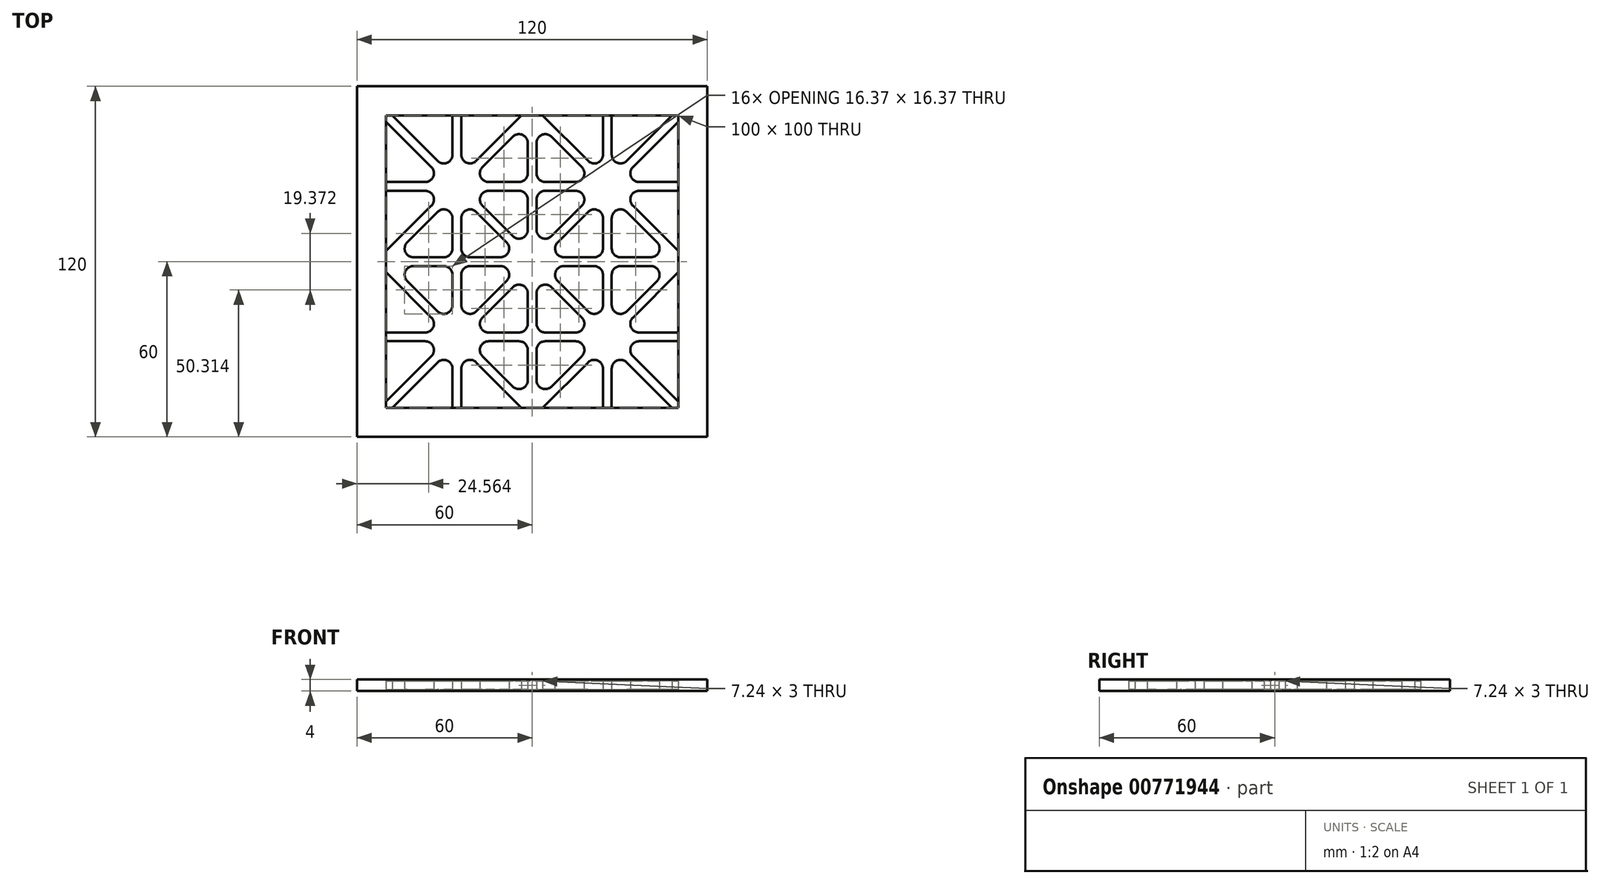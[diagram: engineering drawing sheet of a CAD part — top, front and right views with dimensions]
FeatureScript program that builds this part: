
annotation { "Feature Type Name" : "Feature", "Feature Type Description" : "" }
export const myFeature = defineFeature(function(context is Context, id is Id, definition is map)
    precondition{}
    {
        {
            var Q0;
            Q0=qCreatedBy(makeId("Top.planeOp"),FACE);
            var sketch = newSketch(context, id + "F0", { "sketchPlane" : qUnion([Q0])});
            skLineSegment(sketch, "E0.bottom", {"start": v(0, 0) * mm, "end": v(120, 0) * mm});
            skLineSegment(sketch, "E0.top", {"start": v(0, 120) * mm, "end": v(120, 120) * mm});
            skLineSegment(sketch, "E0.left", {"start": v(0, 0) * mm, "end": v(0, 120) * mm});
            skLineSegment(sketch, "E0.right", {"start": v(120, 0) * mm, "end": v(120, 120) * mm});
            skLineSegment(sketch, "E1.0", {"start": v(10, 10) * mm, "end": v(10, 110) * mm});
            skLineSegment(sketch, "E1.1", {"start": v(10, 10) * mm, "end": v(110, 10) * mm});
            skLineSegment(sketch, "E1.2", {"start": v(110, 10) * mm, "end": v(110, 110) * mm});
            skLineSegment(sketch, "E1.3", {"start": v(10, 110) * mm, "end": v(110, 110) * mm});
            skSolve(sketch);
        }
        {
            var Q0;
            Q0 = qSketchRegion(id + "F0", true);
            extrude(context, id + "F1", {"entities" : qUnion([Q0]), "depth" : 2 * mm, "offsetDistance" : 25 * mm, "hasSecondDirection" : true, "secondDirectionOppositeDirection" : true, "secondDirectionDepth" : 2 * mm});
        }
        {
            var Q0;
            Q0=qCreatedBy(makeId("Top.planeOp"),FACE);
            var sketch = newSketch(context, id + "F2", { "sketchPlane" : qUnion([Q0])});
            skLineSegment(sketch, "E2.0", {"start": v(10, 10) * mm, "end": v(10, 110) * mm, "construction": true});
            skLineSegment(sketch, "E2.1", {"start": v(10, 110) * mm, "end": v(110, 110) * mm, "construction": true});
            skLineSegment(sketch, "E2.2", {"start": v(110, 10) * mm, "end": v(110, 110) * mm, "construction": true});
            skLineSegment(sketch, "E2.3", {"start": v(10, 10) * mm, "end": v(110, 10) * mm, "construction": true});
            skLineSegment(sketch, "E3", {"start": v(10, 60) * mm, "end": v(110, 60) * mm, "construction": true});
            skLineSegment(sketch, "E4", {"start": v(60, 10) * mm, "end": v(60, 110) * mm, "construction": true});
            skLineSegment(sketch, "E5.0", {"start": v(12.12, 58.5) * mm, "end": v(32.75, 58.5) * mm});
            skLineSegment(sketch, "E6.MirrorCS", {"start": v(12.12, 61.5) * mm, "end": v(32.75, 61.5) * mm});
            skLineSegment(sketch, "E7.0", {"start": v(61.5, 10) * mm, "end": v(61.5, 32.75) * mm});
            skLineSegment(sketch, "E8.MirrorCS", {"start": v(58.5, 12.12) * mm, "end": v(58.5, 32.75) * mm});
            skLineSegment(sketch, "E9", {"start": v(10, 10) * mm, "end": v(58.5, 58.5) * mm, "construction": true});
            skLineSegment(sketch, "E10.trimOffspring", {"start": v(58.5, 63.62) * mm, "end": v(58.5, 84.25) * mm});
            skLineSegment(sketch, "E11.trimOffspring", {"start": v(63.62, 58.5) * mm, "end": v(84.25, 58.5) * mm});
            skLineSegment(sketch, "E12.trimOffspring", {"start": v(61.5, 63.62) * mm, "end": v(61.5, 84.25) * mm});
            skLineSegment(sketch, "E13.trimOffspring", {"start": v(63.62, 61.5) * mm, "end": v(84.25, 61.5) * mm});
            skLineSegment(sketch, "E14.0", {"start": v(12.12, 10) * mm, "end": v(32.75, 30.63) * mm});
            skLineSegment(sketch, "E15.MirrorCS", {"start": v(10, 12.12) * mm, "end": v(30.63, 32.75) * mm});
            skLineSegment(sketch, "E16", {"start": v(58.5, 10) * mm, "end": v(35.31, 33.19) * mm, "construction": true});
            skLineSegment(sketch, "E17.0", {"start": v(58.5, 12.12) * mm, "end": v(37.87, 32.75) * mm});
            skLineSegment(sketch, "E18.MirrorCS", {"start": v(56.38, 10) * mm, "end": v(35.75, 30.63) * mm});
            skLineSegment(sketch, "E19.trimOffspring", {"start": v(37.87, 35.75) * mm, "end": v(58.5, 56.38) * mm});
            skLineSegment(sketch, "E20.MirrorCS", {"start": v(12.12, 58.5) * mm, "end": v(32.75, 37.87) * mm});
            skLineSegment(sketch, "E21.MirrorCS", {"start": v(10, 56.38) * mm, "end": v(30.63, 35.75) * mm});
            skLineSegment(sketch, "E22.trimOffspring", {"start": v(35.75, 37.87) * mm, "end": v(56.38, 58.5) * mm});
            skPoint(sketch, "E23.orphan", {"position": v(10, 58.5) * mm});
            skLineSegment(sketch, "E24.1.0", {"start": v(32.75, 58.5) * mm, "end": v(32.75, 37.87) * mm});
            skLineSegment(sketch, "E24.1.2", {"start": v(37.87, 35.75) * mm, "end": v(58.5, 35.75) * mm});
            skLineSegment(sketch, "E24.1.3", {"start": v(37.87, 32.75) * mm, "end": v(58.5, 32.75) * mm});
            skLineSegment(sketch, "E24.1.4", {"start": v(35.75, 10) * mm, "end": v(35.75, 30.63) * mm});
            skLineSegment(sketch, "E24.1.5", {"start": v(32.75, 10) * mm, "end": v(32.75, 30.63) * mm});
            skLineSegment(sketch, "E24.1.6", {"start": v(10, 32.75) * mm, "end": v(30.63, 32.75) * mm});
            skLineSegment(sketch, "E24.1.7", {"start": v(10, 35.75) * mm, "end": v(30.63, 35.75) * mm});
            skPoint(sketch, "E24.center", {"position": v(34.25, 34.25) * mm});
            skLineSegment(sketch, "E24.anchor1", {"start": v(34.25, 34.25) * mm, "end": v(12.12, 10) * mm, "construction": true});
            skLineSegment(sketch, "E24.anchor2", {"start": v(34.25, 34.25) * mm, "end": v(1.46, 32.75) * mm, "construction": true});
            skPoint(sketch, "E25.orphan", {"position": v(32.75, 67.04) * mm});
            skPoint(sketch, "E26.orphan", {"position": v(35.75, 67.04) * mm});
            skLineSegment(sketch, "E27.trimOffspring", {"start": v(35.75, 58.5) * mm, "end": v(56.38, 58.5) * mm});
            skLineSegment(sketch, "E28.trimOffspring", {"start": v(35.75, 58.5) * mm, "end": v(35.75, 37.87) * mm});
            skPoint(sketch, "E29.orphan", {"position": v(67.04, 35.75) * mm});
            skLineSegment(sketch, "E30.trimOffspring", {"start": v(58.5, 35.75) * mm, "end": v(58.5, 56.38) * mm});
            skPoint(sketch, "E31.orphan", {"position": v(32.75, 35.75) * mm});
            skPoint(sketch, "E32.orphan", {"position": v(34.25, 36.37) * mm});
            skPoint(sketch, "E33.orphan", {"position": v(35.75, 35.75) * mm});
            skPoint(sketch, "E34.orphan", {"position": v(36.37, 34.25) * mm});
            skPoint(sketch, "E35.orphan", {"position": v(35.75, 32.75) * mm});
            skPoint(sketch, "E36.orphan", {"position": v(34.25, 32.13) * mm});
            skLineSegment(sketch, "E37.trimOffspring", {"start": v(32.75, 32.6) * mm, "end": v(32.75, 32.75) * mm});
            skLineSegment(sketch, "E38.trimOffspring", {"start": v(32.03, 34.15) * mm, "end": v(32.13, 34.25) * mm});
            skLineSegment(sketch, "E39", {"start": v(10, 35.75) * mm, "end": v(10, 32.75) * mm});
            skPoint(sketch, "E40.orphan", {"position": v(1.46, 35.75) * mm});
            skPoint(sketch, "E41.orphan", {"position": v(35.75, 1.46) * mm});
            skPoint(sketch, "E42.orphan", {"position": v(32.75, 1.46) * mm});
            skLineSegment(sketch, "E43.1.0", {"start": v(107.88, 58.5) * mm, "end": v(87.25, 37.87) * mm});
            skLineSegment(sketch, "E43.1.1", {"start": v(110, 56.38) * mm, "end": v(89.37, 35.75) * mm});
            skLineSegment(sketch, "E43.1.2", {"start": v(110, 35.75) * mm, "end": v(89.37, 35.75) * mm});
            skLineSegment(sketch, "E43.1.3", {"start": v(110, 32.75) * mm, "end": v(89.37, 32.75) * mm});
            skLineSegment(sketch, "E43.1.4", {"start": v(110, 12.12) * mm, "end": v(89.37, 32.75) * mm});
            skLineSegment(sketch, "E43.1.5", {"start": v(107.88, 10) * mm, "end": v(87.25, 30.63) * mm});
            skLineSegment(sketch, "E43.1.6", {"start": v(87.25, 10) * mm, "end": v(87.25, 30.63) * mm});
            skLineSegment(sketch, "E43.1.7", {"start": v(84.25, 10) * mm, "end": v(84.25, 30.63) * mm});
            skLineSegment(sketch, "E43.1.8", {"start": v(63.62, 10) * mm, "end": v(84.25, 30.63) * mm});
            skLineSegment(sketch, "E43.1.9", {"start": v(61.5, 12.12) * mm, "end": v(82.13, 32.75) * mm});
            skLineSegment(sketch, "E43.1.10", {"start": v(61.5, 32.75) * mm, "end": v(82.13, 32.75) * mm});
            skLineSegment(sketch, "E43.1.11", {"start": v(61.5, 35.75) * mm, "end": v(82.13, 35.75) * mm});
            skLineSegment(sketch, "E43.1.12", {"start": v(82.13, 35.75) * mm, "end": v(61.5, 56.38) * mm});
            skLineSegment(sketch, "E43.1.13", {"start": v(84.25, 37.87) * mm, "end": v(63.62, 58.5) * mm});
            skLineSegment(sketch, "E43.1.14", {"start": v(84.25, 37.87) * mm, "end": v(84.25, 58.5) * mm});
            skLineSegment(sketch, "E43.1.15", {"start": v(87.25, 37.87) * mm, "end": v(87.25, 58.5) * mm});
            skLineSegment(sketch, "E43.2.0", {"start": v(61.5, 107.88) * mm, "end": v(82.13, 87.25) * mm});
            skLineSegment(sketch, "E43.2.1", {"start": v(63.62, 110) * mm, "end": v(84.25, 89.37) * mm});
            skLineSegment(sketch, "E43.2.2", {"start": v(84.25, 110) * mm, "end": v(84.25, 89.37) * mm});
            skLineSegment(sketch, "E43.2.3", {"start": v(87.25, 110) * mm, "end": v(87.25, 89.37) * mm});
            skLineSegment(sketch, "E43.2.4", {"start": v(107.88, 110) * mm, "end": v(87.25, 89.37) * mm});
            skLineSegment(sketch, "E43.2.5", {"start": v(110, 107.88) * mm, "end": v(89.37, 87.25) * mm});
            skLineSegment(sketch, "E43.2.6", {"start": v(110, 87.25) * mm, "end": v(89.37, 87.25) * mm});
            skLineSegment(sketch, "E43.2.7", {"start": v(110, 84.25) * mm, "end": v(89.37, 84.25) * mm});
            skLineSegment(sketch, "E43.2.8", {"start": v(110, 63.62) * mm, "end": v(89.37, 84.25) * mm});
            skLineSegment(sketch, "E43.2.9", {"start": v(107.88, 61.5) * mm, "end": v(87.25, 82.13) * mm});
            skLineSegment(sketch, "E43.2.10", {"start": v(87.25, 61.5) * mm, "end": v(87.25, 82.13) * mm});
            skLineSegment(sketch, "E43.2.11", {"start": v(84.25, 61.5) * mm, "end": v(84.25, 82.13) * mm});
            skLineSegment(sketch, "E43.2.12", {"start": v(84.25, 82.13) * mm, "end": v(63.62, 61.5) * mm});
            skLineSegment(sketch, "E43.2.13", {"start": v(82.13, 84.25) * mm, "end": v(61.5, 63.62) * mm});
            skLineSegment(sketch, "E43.2.14", {"start": v(82.13, 84.25) * mm, "end": v(61.5, 84.25) * mm});
            skLineSegment(sketch, "E43.2.15", {"start": v(82.13, 87.25) * mm, "end": v(61.5, 87.25) * mm});
            skLineSegment(sketch, "E43.3.0", {"start": v(12.12, 61.5) * mm, "end": v(32.75, 82.13) * mm});
            skLineSegment(sketch, "E43.3.1", {"start": v(10, 63.62) * mm, "end": v(30.63, 84.25) * mm});
            skLineSegment(sketch, "E43.3.2", {"start": v(10, 84.25) * mm, "end": v(30.63, 84.25) * mm});
            skLineSegment(sketch, "E43.3.3", {"start": v(10, 87.25) * mm, "end": v(30.63, 87.25) * mm});
            skLineSegment(sketch, "E43.3.4", {"start": v(10, 107.88) * mm, "end": v(30.63, 87.25) * mm});
            skLineSegment(sketch, "E43.3.5", {"start": v(12.12, 110) * mm, "end": v(32.75, 89.37) * mm});
            skLineSegment(sketch, "E43.3.6", {"start": v(32.75, 110) * mm, "end": v(32.75, 89.37) * mm});
            skLineSegment(sketch, "E43.3.7", {"start": v(35.75, 110) * mm, "end": v(35.75, 89.37) * mm});
            skLineSegment(sketch, "E43.3.8", {"start": v(56.38, 110) * mm, "end": v(35.75, 89.37) * mm});
            skLineSegment(sketch, "E43.3.9", {"start": v(58.5, 107.88) * mm, "end": v(37.87, 87.25) * mm});
            skLineSegment(sketch, "E43.3.10", {"start": v(58.5, 87.25) * mm, "end": v(37.87, 87.25) * mm});
            skLineSegment(sketch, "E43.3.11", {"start": v(58.5, 84.25) * mm, "end": v(37.87, 84.25) * mm});
            skLineSegment(sketch, "E43.3.12", {"start": v(37.87, 84.25) * mm, "end": v(58.5, 63.62) * mm});
            skLineSegment(sketch, "E43.3.13", {"start": v(35.75, 82.13) * mm, "end": v(56.38, 61.5) * mm});
            skLineSegment(sketch, "E43.3.14", {"start": v(35.75, 82.13) * mm, "end": v(35.75, 61.5) * mm});
            skLineSegment(sketch, "E43.3.15", {"start": v(32.75, 82.13) * mm, "end": v(32.75, 61.5) * mm});
            skPoint(sketch, "E43.center", {"position": v(60, 60) * mm});
            skLineSegment(sketch, "E44.trimOffspring", {"start": v(35.75, 61.5) * mm, "end": v(56.38, 61.5) * mm});
            skLineSegment(sketch, "E45.trimOffspring", {"start": v(58.5, 87.25) * mm, "end": v(58.5, 110) * mm});
            skLineSegment(sketch, "E46.trimOffspring", {"start": v(61.5, 87.25) * mm, "end": v(61.5, 110) * mm});
            skLineSegment(sketch, "E47.trimOffspring", {"start": v(61.5, 35.75) * mm, "end": v(61.5, 56.38) * mm});
            skLineSegment(sketch, "E48.trimOffspring", {"start": v(87.25, 58.5) * mm, "end": v(110, 58.5) * mm});
            skLineSegment(sketch, "E49.trimOffspring", {"start": v(87.25, 61.5) * mm, "end": v(110, 61.5) * mm});
            skLineSegment(sketch, "E50", {"start": v(107.88, 110) * mm, "end": v(110, 110) * mm});
            skLineSegment(sketch, "E51", {"start": v(110, 107.88) * mm, "end": v(110, 110) * mm});
            skLineSegment(sketch, "E52", {"start": v(110, 87.25) * mm, "end": v(110, 84.25) * mm});
            skLineSegment(sketch, "E53", {"start": v(84.25, 110) * mm, "end": v(87.25, 110) * mm});
            skLineSegment(sketch, "E54", {"start": v(56.38, 110) * mm, "end": v(63.62, 110) * mm});
            skLineSegment(sketch, "E55", {"start": v(110, 63.62) * mm, "end": v(110, 56.38) * mm});
            skLineSegment(sketch, "E56", {"start": v(110, 35.75) * mm, "end": v(110, 32.75) * mm});
            skLineSegment(sketch, "E57", {"start": v(107.88, 10) * mm, "end": v(110, 10) * mm});
            skLineSegment(sketch, "E58", {"start": v(110, 12.12) * mm, "end": v(110, 10) * mm});
            skLineSegment(sketch, "E59", {"start": v(84.25, 10) * mm, "end": v(87.25, 10) * mm});
            skLineSegment(sketch, "E60", {"start": v(56.38, 10) * mm, "end": v(63.62, 10) * mm});
            skLineSegment(sketch, "E61", {"start": v(32.75, 10) * mm, "end": v(35.75, 10) * mm});
            skLineSegment(sketch, "E62", {"start": v(10, 12.12) * mm, "end": v(10, 10) * mm});
            skLineSegment(sketch, "E63", {"start": v(10, 10) * mm, "end": v(12.12, 10) * mm});
            skLineSegment(sketch, "E64", {"start": v(10, 63.62) * mm, "end": v(10, 56.38) * mm});
            skPoint(sketch, "E65.orphan", {"position": v(10, 61.5) * mm});
            skLineSegment(sketch, "E66", {"start": v(10, 87.25) * mm, "end": v(10, 84.25) * mm});
            skLineSegment(sketch, "E67", {"start": v(10, 107.88) * mm, "end": v(10, 110) * mm});
            skLineSegment(sketch, "E68", {"start": v(10, 110) * mm, "end": v(12.12, 110) * mm});
            skLineSegment(sketch, "E69", {"start": v(32.75, 110) * mm, "end": v(35.75, 110) * mm});
            skSolve(sketch);
        }
        {
            var Q0;
            Q0 = qSketchRegion(id + "F2", true);
            extrude(context, id + "F3", {"entities" : qUnion([Q0]), "operationType" : NewBodyOperationType.ADD, "depth" : 1.5 * mm, "offsetDistance" : 25 * mm, "hasSecondDirection" : true, "secondDirectionOppositeDirection" : true, "secondDirectionDepth" : 1.5 * mm});
        }
        {
            var Q0;
            Q0=makeQuery(id+"F3.opExtrude","SWEPT_EDGE",EDGE,{"disambiguationData":[OSD([sQuery(id+"F2.wireOp",EDGE,"E43.3.0"),sQuery(id+"F2.wireOp",EDGE,"E43.3.15")])]});
            var Q1;
            Q1=makeQuery(id+"F3.opExtrude","SWEPT_EDGE",EDGE,{"disambiguationData":[OSD([sQuery(id+"F2.wireOp",EDGE,"E10.trimOffspring"),sQuery(id+"F2.wireOp",EDGE,"E43.3.11")])]});
            var Q2;
            Q2=makeQuery(id+"F3.opExtrude","SWEPT_EDGE",EDGE,{"disambiguationData":[OSD([sQuery(id+"F2.wireOp",EDGE,"E14.0"),sQuery(id+"F2.wireOp",EDGE,"E24.1.5")])]});
            var Q3;
            Q3=makeQuery(id+"F3.opExtrude","SWEPT_EDGE",EDGE,{"disambiguationData":[OSD([sQuery(id+"F2.wireOp",EDGE,"E8.MirrorCS"),sQuery(id+"F2.wireOp",EDGE,"E24.1.3")])]});
            var Q4;
            Q4=makeQuery(id+"F3.opExtrude","SWEPT_EDGE",EDGE,{"disambiguationData":[OSD([sQuery(id+"F2.wireOp",EDGE,"E43.2.2"),sQuery(id+"F2.wireOp",EDGE,"E53")])]});
            var Q5;
            Q5=makeQuery(id+"F3.opExtrude","SWEPT_EDGE",EDGE,{"disambiguationData":[OSD([sQuery(id+"F2.wireOp",EDGE,"E43.2.5"),sQuery(id+"F2.wireOp",EDGE,"E51")])]});
            var Q6;
            Q6=makeQuery(id+"F3.opExtrude","SWEPT_EDGE",EDGE,{"disambiguationData":[OSD([sQuery(id+"F2.wireOp",EDGE,"E43.2.7"),sQuery(id+"F2.wireOp",EDGE,"E52")])]});
            var Q7;
            Q7=makeQuery(id+"F3.opExtrude","SWEPT_EDGE",EDGE,{"disambiguationData":[OSD([sQuery(id+"F2.wireOp",EDGE,"E11.trimOffspring"),sQuery(id+"F2.wireOp",EDGE,"E43.1.14")])]});
            var Q8;
            Q8=makeQuery(id+"F3.opExtrude","SWEPT_EDGE",EDGE,{"disambiguationData":[OSD([sQuery(id+"F2.wireOp",EDGE,"E43.1.7"),sQuery(id+"F2.wireOp",EDGE,"E43.1.8")])]});
            var Q9;
            Q9=makeQuery(id+"F3.opExtrude","SWEPT_EDGE",EDGE,{"disambiguationData":[OSD([sQuery(id+"F2.wireOp",EDGE,"E43.3.6"),sQuery(id+"F2.wireOp",EDGE,"E69")])]});
            var Q10;
            Q10=makeQuery(id+"F3.opExtrude","SWEPT_EDGE",EDGE,{"disambiguationData":[OSD([sQuery(id+"F2.wireOp",EDGE,"E5.0"),sQuery(id+"F2.wireOp",EDGE,"E24.1.0")])]});
            var Q11;
            Q11=makeQuery(id+"F3.opExtrude","SWEPT_EDGE",EDGE,{"disambiguationData":[OSD([sQuery(id+"F2.wireOp",EDGE,"E19.trimOffspring"),sQuery(id+"F2.wireOp",EDGE,"E30.trimOffspring")])]});
            var Q12;
            Q12=makeQuery(id+"F3.opExtrude","SWEPT_EDGE",EDGE,{"disambiguationData":[OSD([sQuery(id+"F2.wireOp",EDGE,"E27.trimOffspring"),sQuery(id+"F2.wireOp",EDGE,"E28.trimOffspring")])]});
            var Q13;
            Q13=makeQuery(id+"F3.opExtrude","SWEPT_EDGE",EDGE,{"disambiguationData":[OSD([sQuery(id+"F2.wireOp",EDGE,"E43.3.5"),sQuery(id+"F2.wireOp",EDGE,"E68")])]});
            var Q14;
            Q14=makeQuery(id+"F3.opExtrude","SWEPT_EDGE",EDGE,{"disambiguationData":[OSD([sQuery(id+"F2.wireOp",EDGE,"E43.3.2"),sQuery(id+"F2.wireOp",EDGE,"E66")])]});
            var Q15;
            Q15=makeQuery(id+"F3.opExtrude","SWEPT_EDGE",EDGE,{"disambiguationData":[OSD([sQuery(id+"F2.wireOp",EDGE,"E24.1.6"),sQuery(id+"F2.wireOp",EDGE,"E39")])]});
            var Q16;
            Q16=makeQuery(id+"F3.opExtrude","SWEPT_EDGE",EDGE,{"disambiguationData":[OSD([sQuery(id+"F2.wireOp",EDGE,"E7.0"),sQuery(id+"F2.wireOp",EDGE,"E43.1.10")])]});
            var Q17;
            Q17=makeQuery(id+"F3.opExtrude","SWEPT_EDGE",EDGE,{"disambiguationData":[OSD([sQuery(id+"F2.wireOp",EDGE,"E43.3.7"),sQuery(id+"F2.wireOp",EDGE,"E69")])]});
            var Q18;
            Q18=makeQuery(id+"F3.opExtrude","SWEPT_EDGE",EDGE,{"disambiguationData":[OSD([sQuery(id+"F2.wireOp",EDGE,"E43.2.3"),sQuery(id+"F2.wireOp",EDGE,"E53")])]});
            var Q19;
            Q19=makeQuery(id+"F3.opExtrude","SWEPT_EDGE",EDGE,{"disambiguationData":[OSD([sQuery(id+"F2.wireOp",EDGE,"E12.trimOffspring"),sQuery(id+"F2.wireOp",EDGE,"E43.2.14")])]});
            var Q20;
            Q20=makeQuery(id+"F3.opExtrude","SWEPT_EDGE",EDGE,{"disambiguationData":[OSD([sQuery(id+"F2.wireOp",EDGE,"E43.1.12"),sQuery(id+"F2.wireOp",EDGE,"E47.trimOffspring")])]});
            var Q21;
            Q21=makeQuery(id+"F3.opExtrude","SWEPT_EDGE",EDGE,{"disambiguationData":[OSD([sQuery(id+"F2.wireOp",EDGE,"E43.2.0"),sQuery(id+"F2.wireOp",EDGE,"E46.trimOffspring")])]});
            var Q22;
            Q22=makeQuery(id+"F3.opExtrude","SWEPT_EDGE",EDGE,{"disambiguationData":[OSD([sQuery(id+"F2.wireOp",EDGE,"E43.2.9"),sQuery(id+"F2.wireOp",EDGE,"E43.2.10")])]});
            var Q23;
            Q23=makeQuery(id+"F3.opExtrude","SWEPT_EDGE",EDGE,{"disambiguationData":[OSD([sQuery(id+"F2.wireOp",EDGE,"E43.1.15"),sQuery(id+"F2.wireOp",EDGE,"E48.trimOffspring")])]});
            var Q24;
            Q24=makeQuery(id+"F3.opExtrude","SWEPT_EDGE",EDGE,{"disambiguationData":[OSD([sQuery(id+"F2.wireOp",EDGE,"E43.1.5"),sQuery(id+"F2.wireOp",EDGE,"E43.1.6")])]});
            var Q25;
            Q25=makeQuery(id+"F3.opExtrude","SWEPT_EDGE",EDGE,{"disambiguationData":[OSD([sQuery(id+"F2.wireOp",EDGE,"E18.MirrorCS"),sQuery(id+"F2.wireOp",EDGE,"E24.1.4")])]});
            var Q26;
            Q26=makeQuery(id+"F3.opExtrude","SWEPT_EDGE",EDGE,{"disambiguationData":[OSD([sQuery(id+"F2.wireOp",EDGE,"E43.3.4"),sQuery(id+"F2.wireOp",EDGE,"E67")])]});
            var Q27;
            Q27=makeQuery(id+"F3.opExtrude","SWEPT_EDGE",EDGE,{"disambiguationData":[OSD([sQuery(id+"F2.wireOp",EDGE,"E21.MirrorCS"),sQuery(id+"F2.wireOp",EDGE,"E64")])]});
            var Q28;
            Q28=makeQuery(id+"F3.opExtrude","SWEPT_EDGE",EDGE,{"disambiguationData":[OSD([sQuery(id+"F2.wireOp",EDGE,"E11.trimOffspring"),sQuery(id+"F2.wireOp",EDGE,"E43.1.13")])]});
            var Q29;
            Q29=makeQuery(id+"F3.opExtrude","SWEPT_EDGE",EDGE,{"disambiguationData":[OSD([sQuery(id+"F2.wireOp",EDGE,"E17.0"),sQuery(id+"F2.wireOp",EDGE,"E24.1.3")])]});
            var Q30;
            Q30=makeQuery(id+"F3.opExtrude","SWEPT_EDGE",EDGE,{"disambiguationData":[OSD([sQuery(id+"F2.wireOp",EDGE,"E43.1.3"),sQuery(id+"F2.wireOp",EDGE,"E43.1.4")])]});
            var Q31;
            Q31=makeQuery(id+"F3.opExtrude","SWEPT_EDGE",EDGE,{"disambiguationData":[OSD([sQuery(id+"F2.wireOp",EDGE,"E43.2.7"),sQuery(id+"F2.wireOp",EDGE,"E43.2.8")])]});
            var Q32;
            Q32=makeQuery(id+"F3.opExtrude","SWEPT_EDGE",EDGE,{"disambiguationData":[OSD([sQuery(id+"F2.wireOp",EDGE,"E43.3.11"),sQuery(id+"F2.wireOp",EDGE,"E43.3.12")])]});
            var Q33;
            Q33=makeQuery(id+"F3.opExtrude","SWEPT_EDGE",EDGE,{"disambiguationData":[OSD([sQuery(id+"F2.wireOp",EDGE,"E43.2.1"),sQuery(id+"F2.wireOp",EDGE,"E54")])]});
            var Q34;
            Q34=makeQuery(id+"F3.opExtrude","SWEPT_EDGE",EDGE,{"disambiguationData":[OSD([sQuery(id+"F2.wireOp",EDGE,"E43.3.8"),sQuery(id+"F2.wireOp",EDGE,"E54")])]});
            var Q35;
            Q35=makeQuery(id+"F3.opExtrude","SWEPT_EDGE",EDGE,{"disambiguationData":[OSD([sQuery(id+"F2.wireOp",EDGE,"E43.2.13"),sQuery(id+"F2.wireOp",EDGE,"E43.2.14")])]});
            var Q36;
            Q36=makeQuery(id+"F3.opExtrude","SWEPT_EDGE",EDGE,{"disambiguationData":[OSD([sQuery(id+"F2.wireOp",EDGE,"E43.3.1"),sQuery(id+"F2.wireOp",EDGE,"E43.3.2")])]});
            var Q37;
            Q37=makeQuery(id+"F3.opExtrude","SWEPT_EDGE",EDGE,{"disambiguationData":[OSD([sQuery(id+"F2.wireOp",EDGE,"E15.MirrorCS"),sQuery(id+"F2.wireOp",EDGE,"E24.1.6")])]});
            var Q38;
            Q38=makeQuery(id+"F3.opExtrude","SWEPT_EDGE",EDGE,{"disambiguationData":[OSD([sQuery(id+"F2.wireOp",EDGE,"E43.1.9"),sQuery(id+"F2.wireOp",EDGE,"E43.1.10")])]});
            var Q39;
            Q39=makeQuery(id+"F3.opExtrude","SWEPT_EDGE",EDGE,{"disambiguationData":[OSD([sQuery(id+"F2.wireOp",EDGE,"E43.1.3"),sQuery(id+"F2.wireOp",EDGE,"E56")])]});
            var Q40;
            Q40=makeQuery(id+"F3.opExtrude","SWEPT_EDGE",EDGE,{"disambiguationData":[OSD([sQuery(id+"F2.wireOp",EDGE,"E43.1.0"),sQuery(id+"F2.wireOp",EDGE,"E48.trimOffspring")])]});
            var Q41;
            Q41=makeQuery(id+"F3.opExtrude","SWEPT_EDGE",EDGE,{"disambiguationData":[OSD([sQuery(id+"F2.wireOp",EDGE,"E24.1.7"),sQuery(id+"F2.wireOp",EDGE,"E39")])]});
            var Q42;
            Q42=makeQuery(id+"F3.opExtrude","SWEPT_EDGE",EDGE,{"disambiguationData":[OSD([sQuery(id+"F2.wireOp",EDGE,"E43.3.3"),sQuery(id+"F2.wireOp",EDGE,"E66")])]});
            var Q43;
            Q43=makeQuery(id+"F3.opExtrude","SWEPT_EDGE",EDGE,{"disambiguationData":[OSD([sQuery(id+"F2.wireOp",EDGE,"E24.1.4"),sQuery(id+"F2.wireOp",EDGE,"E61")])]});
            var Q44;
            Q44=makeQuery(id+"F3.opExtrude","SWEPT_EDGE",EDGE,{"disambiguationData":[OSD([sQuery(id+"F2.wireOp",EDGE,"E43.1.6"),sQuery(id+"F2.wireOp",EDGE,"E59")])]});
            var Q45;
            Q45=makeQuery(id+"F3.opExtrude","SWEPT_EDGE",EDGE,{"disambiguationData":[OSD([sQuery(id+"F2.wireOp",EDGE,"E19.trimOffspring"),sQuery(id+"F2.wireOp",EDGE,"E24.1.2")])]});
            var Q46;
            Q46=makeQuery(id+"F3.opExtrude","SWEPT_EDGE",EDGE,{"disambiguationData":[OSD([sQuery(id+"F2.wireOp",EDGE,"E43.1.1"),sQuery(id+"F2.wireOp",EDGE,"E43.1.2")])]});
            var Q47;
            Q47=makeQuery(id+"F3.opExtrude","SWEPT_EDGE",EDGE,{"disambiguationData":[OSD([sQuery(id+"F2.wireOp",EDGE,"E43.2.10"),sQuery(id+"F2.wireOp",EDGE,"E49.trimOffspring")])]});
            var Q48;
            Q48=makeQuery(id+"F3.opExtrude","SWEPT_EDGE",EDGE,{"disambiguationData":[OSD([sQuery(id+"F2.wireOp",EDGE,"E43.3.14"),sQuery(id+"F2.wireOp",EDGE,"E44.trimOffspring")])]});
            var Q49;
            Q49=makeQuery(id+"F3.opExtrude","SWEPT_EDGE",EDGE,{"disambiguationData":[OSD([sQuery(id+"F2.wireOp",EDGE,"E43.2.15"),sQuery(id+"F2.wireOp",EDGE,"E46.trimOffspring")])]});
            var Q50;
            Q50=makeQuery(id+"F3.opExtrude","SWEPT_EDGE",EDGE,{"disambiguationData":[OSD([sQuery(id+"F2.wireOp",EDGE,"E43.2.5"),sQuery(id+"F2.wireOp",EDGE,"E43.2.6")])]});
            var Q51;
            Q51=makeQuery(id+"F3.opExtrude","SWEPT_EDGE",EDGE,{"disambiguationData":[OSD([sQuery(id+"F2.wireOp",EDGE,"E43.3.9"),sQuery(id+"F2.wireOp",EDGE,"E43.3.10")])]});
            var Q52;
            Q52=makeQuery(id+"F3.opExtrude","SWEPT_EDGE",EDGE,{"disambiguationData":[OSD([sQuery(id+"F2.wireOp",EDGE,"E6.MirrorCS"),sQuery(id+"F2.wireOp",EDGE,"E43.3.0")])]});
            var Q53;
            Q53=makeQuery(id+"F3.opExtrude","SWEPT_EDGE",EDGE,{"disambiguationData":[OSD([sQuery(id+"F2.wireOp",EDGE,"E14.0"),sQuery(id+"F2.wireOp",EDGE,"E63")])]});
            var Q54;
            Q54=makeQuery(id+"F3.opExtrude","SWEPT_EDGE",EDGE,{"disambiguationData":[OSD([sQuery(id+"F2.wireOp",EDGE,"E43.1.8"),sQuery(id+"F2.wireOp",EDGE,"E60")])]});
            var Q55;
            Q55=makeQuery(id+"F3.opExtrude","SWEPT_EDGE",EDGE,{"disambiguationData":[OSD([sQuery(id+"F2.wireOp",EDGE,"E43.1.7"),sQuery(id+"F2.wireOp",EDGE,"E59")])]});
            var Q56;
            Q56=makeQuery(id+"F3.opExtrude","SWEPT_EDGE",EDGE,{"disambiguationData":[OSD([sQuery(id+"F2.wireOp",EDGE,"E18.MirrorCS"),sQuery(id+"F2.wireOp",EDGE,"E60")])]});
            var Q57;
            Q57=makeQuery(id+"F3.opExtrude","SWEPT_EDGE",EDGE,{"disambiguationData":[OSD([sQuery(id+"F2.wireOp",EDGE,"E24.1.5"),sQuery(id+"F2.wireOp",EDGE,"E61")])]});
            var Q58;
            Q58=makeQuery(id+"F3.opExtrude","SWEPT_EDGE",EDGE,{"disambiguationData":[OSD([sQuery(id+"F2.wireOp",EDGE,"E21.MirrorCS"),sQuery(id+"F2.wireOp",EDGE,"E24.1.7")])]});
            var Q59;
            Q59=makeQuery(id+"F3.opExtrude","SWEPT_EDGE",EDGE,{"disambiguationData":[OSD([sQuery(id+"F2.wireOp",EDGE,"E24.1.2"),sQuery(id+"F2.wireOp",EDGE,"E30.trimOffspring")])]});
            var Q60;
            Q60=makeQuery(id+"F3.opExtrude","SWEPT_EDGE",EDGE,{"disambiguationData":[OSD([sQuery(id+"F2.wireOp",EDGE,"E43.3.10"),sQuery(id+"F2.wireOp",EDGE,"E45.trimOffspring")])]});
            var Q61;
            Q61=makeQuery(id+"F3.opExtrude","SWEPT_EDGE",EDGE,{"disambiguationData":[OSD([sQuery(id+"F2.wireOp",EDGE,"E43.1.11"),sQuery(id+"F2.wireOp",EDGE,"E43.1.12")])]});
            var Q62;
            Q62=makeQuery(id+"F3.opExtrude","SWEPT_EDGE",EDGE,{"disambiguationData":[OSD([sQuery(id+"F2.wireOp",EDGE,"E43.1.2"),sQuery(id+"F2.wireOp",EDGE,"E56")])]});
            var Q63;
            Q63=makeQuery(id+"F3.opExtrude","SWEPT_EDGE",EDGE,{"disambiguationData":[OSD([sQuery(id+"F2.wireOp",EDGE,"E43.2.6"),sQuery(id+"F2.wireOp",EDGE,"E52")])]});
            var Q64;
            Q64=makeQuery(id+"F3.opExtrude","SWEPT_EDGE",EDGE,{"disambiguationData":[OSD([sQuery(id+"F2.wireOp",EDGE,"E43.1.11"),sQuery(id+"F2.wireOp",EDGE,"E47.trimOffspring")])]});
            var Q65;
            Q65=makeQuery(id+"F3.opExtrude","SWEPT_EDGE",EDGE,{"disambiguationData":[OSD([sQuery(id+"F2.wireOp",EDGE,"E6.MirrorCS"),sQuery(id+"F2.wireOp",EDGE,"E43.3.15")])]});
            var Q66;
            Q66=makeQuery(id+"F3.opExtrude","SWEPT_EDGE",EDGE,{"disambiguationData":[OSD([sQuery(id+"F2.wireOp",EDGE,"E13.trimOffspring"),sQuery(id+"F2.wireOp",EDGE,"E43.2.11")])]});
            var Q67;
            Q67=makeQuery(id+"F3.opExtrude","SWEPT_EDGE",EDGE,{"disambiguationData":[OSD([sQuery(id+"F2.wireOp",EDGE,"E43.1.0"),sQuery(id+"F2.wireOp",EDGE,"E43.1.15")])]});
            var Q68;
            Q68=makeQuery(id+"F3.opExtrude","SWEPT_EDGE",EDGE,{"disambiguationData":[OSD([sQuery(id+"F2.wireOp",EDGE,"E43.2.3"),sQuery(id+"F2.wireOp",EDGE,"E43.2.4")])]});
            var Q69;
            Q69=makeQuery(id+"F3.opExtrude","SWEPT_EDGE",EDGE,{"disambiguationData":[OSD([sQuery(id+"F2.wireOp",EDGE,"E22.trimOffspring"),sQuery(id+"F2.wireOp",EDGE,"E28.trimOffspring")])]});
            var Q70;
            Q70=makeQuery(id+"F3.opExtrude","SWEPT_EDGE",EDGE,{"disambiguationData":[OSD([sQuery(id+"F2.wireOp",EDGE,"E43.3.7"),sQuery(id+"F2.wireOp",EDGE,"E43.3.8")])]});
            var Q71;
            Q71=makeQuery(id+"F3.opExtrude","SWEPT_EDGE",EDGE,{"disambiguationData":[OSD([sQuery(id+"F2.wireOp",EDGE,"E43.3.3"),sQuery(id+"F2.wireOp",EDGE,"E43.3.4")])]});
            var Q72;
            Q72=makeQuery(id+"F3.opExtrude","SWEPT_EDGE",EDGE,{"disambiguationData":[OSD([sQuery(id+"F2.wireOp",EDGE,"E43.2.0"),sQuery(id+"F2.wireOp",EDGE,"E43.2.15")])]});
            var Q73;
            Q73=makeQuery(id+"F3.opExtrude","SWEPT_EDGE",EDGE,{"disambiguationData":[OSD([sQuery(id+"F2.wireOp",EDGE,"E43.3.13"),sQuery(id+"F2.wireOp",EDGE,"E44.trimOffspring")])]});
            var Q74;
            Q74=makeQuery(id+"F3.opExtrude","SWEPT_EDGE",EDGE,{"disambiguationData":[OSD([sQuery(id+"F2.wireOp",EDGE,"E13.trimOffspring"),sQuery(id+"F2.wireOp",EDGE,"E43.2.12")])]});
            var Q75;
            Q75=makeQuery(id+"F3.opExtrude","SWEPT_EDGE",EDGE,{"disambiguationData":[OSD([sQuery(id+"F2.wireOp",EDGE,"E43.3.1"),sQuery(id+"F2.wireOp",EDGE,"E64")])]});
            var Q76;
            Q76=makeQuery(id+"F3.opExtrude","SWEPT_EDGE",EDGE,{"disambiguationData":[OSD([sQuery(id+"F2.wireOp",EDGE,"E43.2.1"),sQuery(id+"F2.wireOp",EDGE,"E43.2.2")])]});
            var Q77;
            Q77=makeQuery(id+"F3.opExtrude","SWEPT_EDGE",EDGE,{"disambiguationData":[OSD([sQuery(id+"F2.wireOp",EDGE,"E5.0"),sQuery(id+"F2.wireOp",EDGE,"E20.MirrorCS")])]});
            var Q78;
            Q78=makeQuery(id+"F3.opExtrude","SWEPT_EDGE",EDGE,{"disambiguationData":[OSD([sQuery(id+"F2.wireOp",EDGE,"E15.MirrorCS"),sQuery(id+"F2.wireOp",EDGE,"E62")])]});
            var Q79;
            Q79=makeQuery(id+"F3.opExtrude","SWEPT_EDGE",EDGE,{"disambiguationData":[OSD([sQuery(id+"F2.wireOp",EDGE,"E43.1.13"),sQuery(id+"F2.wireOp",EDGE,"E43.1.14")])]});
            var Q80;
            Q80=makeQuery(id+"F3.opExtrude","SWEPT_EDGE",EDGE,{"disambiguationData":[OSD([sQuery(id+"F2.wireOp",EDGE,"E43.3.5"),sQuery(id+"F2.wireOp",EDGE,"E43.3.6")])]});
            var Q81;
            Q81=makeQuery(id+"F3.opExtrude","SWEPT_EDGE",EDGE,{"disambiguationData":[OSD([sQuery(id+"F2.wireOp",EDGE,"E20.MirrorCS"),sQuery(id+"F2.wireOp",EDGE,"E24.1.0")])]});
            var Q82;
            Q82=makeQuery(id+"F3.opExtrude","SWEPT_EDGE",EDGE,{"disambiguationData":[OSD([sQuery(id+"F2.wireOp",EDGE,"E43.1.4"),sQuery(id+"F2.wireOp",EDGE,"E58")])]});
            var Q83;
            Q83=makeQuery(id+"F3.opExtrude","SWEPT_EDGE",EDGE,{"disambiguationData":[OSD([sQuery(id+"F2.wireOp",EDGE,"E43.1.5"),sQuery(id+"F2.wireOp",EDGE,"E57")])]});
            var Q84;
            Q84=makeQuery(id+"F3.opExtrude","SWEPT_EDGE",EDGE,{"disambiguationData":[OSD([sQuery(id+"F2.wireOp",EDGE,"E43.2.9"),sQuery(id+"F2.wireOp",EDGE,"E49.trimOffspring")])]});
            var Q85;
            Q85=makeQuery(id+"F3.opExtrude","SWEPT_EDGE",EDGE,{"disambiguationData":[OSD([sQuery(id+"F2.wireOp",EDGE,"E43.2.4"),sQuery(id+"F2.wireOp",EDGE,"E50")])]});
            var Q86;
            Q86=makeQuery(id+"F3.opExtrude","SWEPT_EDGE",EDGE,{"disambiguationData":[OSD([sQuery(id+"F2.wireOp",EDGE,"E8.MirrorCS"),sQuery(id+"F2.wireOp",EDGE,"E17.0")])]});
            var Q87;
            Q87=makeQuery(id+"F3.opExtrude","SWEPT_EDGE",EDGE,{"disambiguationData":[OSD([sQuery(id+"F2.wireOp",EDGE,"E7.0"),sQuery(id+"F2.wireOp",EDGE,"E43.1.9")])]});
            var Q88;
            Q88=makeQuery(id+"F3.opExtrude","SWEPT_EDGE",EDGE,{"disambiguationData":[OSD([sQuery(id+"F2.wireOp",EDGE,"E12.trimOffspring"),sQuery(id+"F2.wireOp",EDGE,"E43.2.13")])]});
            var Q89;
            Q89=makeQuery(id+"F3.opExtrude","SWEPT_EDGE",EDGE,{"disambiguationData":[OSD([sQuery(id+"F2.wireOp",EDGE,"E10.trimOffspring"),sQuery(id+"F2.wireOp",EDGE,"E43.3.12")])]});
            var Q90;
            Q90=makeQuery(id+"F3.opExtrude","SWEPT_EDGE",EDGE,{"disambiguationData":[OSD([sQuery(id+"F2.wireOp",EDGE,"E43.1.1"),sQuery(id+"F2.wireOp",EDGE,"E55")])]});
            var Q91;
            Q91=makeQuery(id+"F3.opExtrude","SWEPT_EDGE",EDGE,{"disambiguationData":[OSD([sQuery(id+"F2.wireOp",EDGE,"E43.2.8"),sQuery(id+"F2.wireOp",EDGE,"E55")])]});
            var Q92;
            Q92=makeQuery(id+"F3.opExtrude","SWEPT_EDGE",EDGE,{"disambiguationData":[OSD([sQuery(id+"F2.wireOp",EDGE,"E22.trimOffspring"),sQuery(id+"F2.wireOp",EDGE,"E27.trimOffspring")])]});
            var Q93;
            Q93=makeQuery(id+"F3.opExtrude","SWEPT_EDGE",EDGE,{"disambiguationData":[OSD([sQuery(id+"F2.wireOp",EDGE,"E43.3.13"),sQuery(id+"F2.wireOp",EDGE,"E43.3.14")])]});
            var Q94;
            Q94=makeQuery(id+"F3.opExtrude","SWEPT_EDGE",EDGE,{"disambiguationData":[OSD([sQuery(id+"F2.wireOp",EDGE,"E43.2.11"),sQuery(id+"F2.wireOp",EDGE,"E43.2.12")])]});
            var Q95;
            Q95=makeQuery(id+"F3.opExtrude","SWEPT_EDGE",EDGE,{"disambiguationData":[OSD([sQuery(id+"F2.wireOp",EDGE,"E43.3.9"),sQuery(id+"F2.wireOp",EDGE,"E45.trimOffspring")])]});
            fillet(context, id + "F4", {"entities" : qUnion([Q0, Q1, Q2, Q3, Q4, Q5, Q6, Q7, Q8, Q9, Q10, Q11, Q12, Q13, Q14, Q15, Q16, Q17, Q18, Q19, Q20, Q21, Q22, Q23, Q24, Q25, Q26, Q27, Q28, Q29, Q30, Q31, Q32, Q33, Q34, Q35, Q36, Q37, Q38, Q39, Q40, Q41, Q42, Q43, Q44, Q45, Q46, Q47, Q48, Q49, Q50, Q51, Q52, Q53, Q54, Q55, Q56, Q57, Q58, Q59, Q60, Q61, Q62, Q63, Q64, Q65, Q66, Q67, Q68, Q69, Q70, Q71, Q72, Q73, Q74, Q75, Q76, Q77, Q78, Q79, Q80, Q81, Q82, Q83, Q84, Q85, Q86, Q87, Q88, Q89, Q90, Q91, Q92, Q93, Q94, Q95]), "radius" : 3 * mm, "tangentPropagation" : true, "allowEdgeOverflow" : false});
        }
    });
